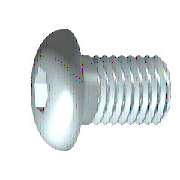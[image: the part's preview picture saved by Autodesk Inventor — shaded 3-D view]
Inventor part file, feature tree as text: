
AUTODESK INVENTOR PART (.ipt)
format: ipt  version: 2024 (Build 280153000, 153)  size: 198,656 bytes
history: native  units: mm (DEFAULTED — no unit token found)
features: extrude x1, plane x1, fillet x1, thread x1
ambient origin geometry x7: Origin, YZ Plane, XY Plane, X Axis, Y Axis, Z Axis, Center Point
bodies: Solid1 (feature_tree), Body (feature_tree)
feature tree (4):
  extrude  "Slot"  Depth=4.5mm
  plane  "Work Plane1"
  fillet  "Fillet2"  Radius=0.306825mm
  thread  "Thread2"  [1 undecoded]
note: 1 required parameter value undecoded (feature->parameter linkage not recoverable at this tier; creation-order binding heuristic only, values carry confidence <= 0.55)
